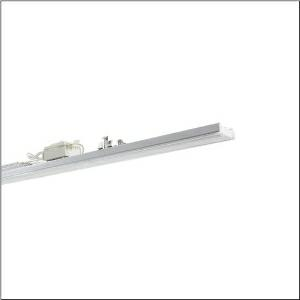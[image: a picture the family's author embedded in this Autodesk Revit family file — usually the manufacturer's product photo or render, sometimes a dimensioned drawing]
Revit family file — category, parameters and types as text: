
# Revit family: licross_11_recessed_mo_51te12dn4axg3c
name_source: partatom
category: Lighting Fixtures
units: mm (PartAtom-declared; Revit-internal decimal feet)

## family parameters
Cut with Voids When Loaded = No
Host = Face
Light Source = No
Part Type = Normal
Room Calculation Point = No
Round Connector Dimension = Use Diameter
Shared = No

## types (1)
- --- (1 x LED, 1010 lm, 6.7 W, 4000K)
    Apparent Load = 7 VA
    CIE Flux Codes = 67 92 99 100 100
    Color Rendering = 80
    Color Temperature = 4000K
    Default Elevation = 1800 mm
    Description = Licross 11 Recessed MO, luminaire insert, of sheet steel, galvanised, coil coated, white, length: 1.500mm, width: 66mm, height: 67mm, LED rated luminous flux: 10.240lm, light colour: 840, SDCM (Standard Deviation of Colour Matching)MacAdam ≤ 2 SDCM (initial), control gear: DALI 2 (for two DALI lines), with plug, 6-pole, with phase selection, for trunking rail, 14-core, mains connection: 220..240V, AC, 50/60Hz, rated input power: 61W, for trunking rail, 14-core, internal wiring halogen-free, for emergency light function, converter,control gear: single battery element, battery: LiFePO4, 9Ah, primary optical cover: cover, of PMMA, light emission: direct distribution, primary light characteristic: symmetric, protection rating (complete): IP54, insulation class (complete): insulation class I (protective earthing), certification: CE, UKCA, protection symbol: D if used in an environment with non-conductive dust loads with corresponding accessories, impact resistance: IK06, permissible ambient temperature for indoor applications: +5..+35°C, standard: EN 60598-2-22, LABS conformity tested according to VDMA 24364:2018-05, reducing of maximum allowable ambient temperature of 5°C with ceiling mounting, corresponds to IFS (International Featured Standards) requirements for safety and quality in the food industry, The light source and the operating device comply with the requirements of the Ecodesign Regulation (EU) 2019/2020 and are replaceable in accordance with this regulation, packaging unit: 1 piece
    Height = 58 mm
    Lamp = 1 x LED
    Lamp Light Flux = 1010 lm
    Lamp Power = 6.7 W
    Lamp count = 1
    Length = 1500 mm
    Luminous efficacy = 151 lm/W
    Manufacturer = Siteco
    ModVariant = No
    Model = 51TE12DN4AXG3C
    Mounting Place = Ceiling
    Mounting Type = Pendant
    Number of Poles = 1
    OnlyDefault = Yes
    Power Factor = 1
    Product Name = Licross 11 Recessed MO
    Product group = luminaire insert | ceiling pendant
    ProductGroupID = 901
    Protection Class = Protection class I
    Protection Degree = IP 54
    RLX_Detail_Level = 1
    RLX_Emergency_Light_Flux = 0 lm
    RLX_Emergency_Type = 0
    RLX_Emergency_Type_DB = No
    RlxData = <blob elided: 25077 chars, md5=a90c954e>
    Socket = socket
    Standby Power = 0 W
    System Light Flux = 1010 lm
    System Power = 7 W
    Type Comments = : emergency light operation: 3 h
    Type Image = l_1296930.jpg
    URL = http://relux.com
    VarID = @adj_094103
    Voltage = 0 V
    Weight = 0.00 kg
    Width = 66 mm

## geometry (parser evidence)
native form markers: Blend x4, Sweep x12
no freeform markers — native parametric forms only
